FCSTD DOCUMENT  (FreeCAD 0.17R11237 (Git))
Label: Box_Latest
License: All rights reserved
LicenseURL: http://en.wikipedia.org/wiki/All_rights_reserved
objects: Sketcher::SketchObject×1
note: 1 computed .brp shape members not serialized (recipe doc carries the construction recipe); baked Part::Feature solids carry a one-line shape summary decoded from their .brp

FEATURE [Sketcher::SketchObject] Sketch
  sketch-geometry (58):
    g0: LineSegment StartX=-50.2046 StartY=69.3306 StartZ=0 EndX=39.7954 EndY=69.3306 EndZ=0
    g1: LineSegment StartX=39.7954 StartY=69.3306 StartZ=0 EndX=39.7954 EndY=-70.6694 EndZ=0
    g2: LineSegment StartX=39.7954 StartY=-70.6694 StartZ=0 EndX=-50.2046 EndY=-70.6694 EndZ=0
    g3: LineSegment StartX=-50.2046 StartY=-70.6694 StartZ=0 EndX=-50.2046 EndY=69.3306 EndZ=0
    g4: LineSegment StartX=-20 StartY=-57.6694 StartZ=0 EndX=10 EndY=-57.6694 EndZ=0
    g5: LineSegment StartX=10 StartY=-57.6694 StartZ=0 EndX=10 EndY=-53.6694 EndZ=0
    g6: LineSegment StartX=10 StartY=-53.6694 StartZ=0 EndX=-20 EndY=-53.6694 EndZ=0
    g7: LineSegment StartX=-20 StartY=-53.6694 StartZ=0 EndX=-20 EndY=-57.6694 EndZ=0
    g8: LineSegment StartX=-40.7046 StartY=56.7181 StartZ=0 EndX=30.2954 EndY=56.7181 EndZ=0
    g9: LineSegment StartX=30.2954 StartY=56.7181 StartZ=0 EndX=30.2954 EndY=32.7181 EndZ=0
    g10: LineSegment StartX=30.2954 StartY=32.7181 StartZ=0 EndX=-40.7046 EndY=32.7181 EndZ=0
    g11: LineSegment StartX=-40.7046 StartY=32.7181 StartZ=0 EndX=-40.7046 EndY=56.7181 EndZ=0
    g12: LineSegment StartX=49.7553 StartY=63.8027 StartZ=0 EndX=79.7553 EndY=63.8027 EndZ=0
    g13: LineSegment StartX=79.7553 StartY=63.8027 StartZ=0 EndX=79.7553 EndY=-66.1973 EndZ=0
    g14: LineSegment StartX=79.7553 StartY=-66.1973 StartZ=0 EndX=49.7553 EndY=-66.1973 EndZ=0
    g15: LineSegment StartX=49.7553 StartY=-66.1973 StartZ=0 EndX=49.7553 EndY=63.8027 EndZ=0
    g16: LineSegment StartX=-60 StartY=63.8027 StartZ=0 EndX=-90 EndY=63.8027 EndZ=0
    g17: LineSegment StartX=-90 StartY=63.8027 StartZ=0 EndX=-90 EndY=-66.1973 EndZ=0
    g18: LineSegment StartX=-90 StartY=-66.1973 StartZ=0 EndX=-60 EndY=-66.1973 EndZ=0
    g19: LineSegment StartX=-60 StartY=-66.1973 StartZ=0 EndX=-60 EndY=63.8027 EndZ=0
    g20: LineSegment StartX=-50 StartY=80 StartZ=0 EndX=40 EndY=80 EndZ=0
    g21: LineSegment StartX=40 StartY=80 StartZ=0 EndX=40 EndY=110 EndZ=0
    g22: LineSegment StartX=40 StartY=110 StartZ=0 EndX=-50 EndY=110 EndZ=0
    g23: LineSegment StartX=-50 StartY=110 StartZ=0 EndX=-50 EndY=80 EndZ=0
    g24: LineSegment StartX=-50 StartY=-80 StartZ=0 EndX=40 EndY=-80 EndZ=0
    g25: LineSegment StartX=40 StartY=-80 StartZ=0 EndX=40 EndY=-110 EndZ=0
    g26: LineSegment StartX=40 StartY=-110 StartZ=0 EndX=-50 EndY=-110 EndZ=0
    g27: LineSegment StartX=-50 StartY=-110 StartZ=0 EndX=-50 EndY=-80 EndZ=0
    g28: LineSegment StartX=90.013 StartY=70 StartZ=0 EndX=180.013 EndY=70 EndZ=0
    g29: LineSegment StartX=180.013 StartY=70 StartZ=0 EndX=180.013 EndY=-70 EndZ=0
    g30: LineSegment StartX=180.013 StartY=-70 StartZ=0 EndX=90.013 EndY=-70 EndZ=0
    g31: LineSegment StartX=90.013 StartY=-70 StartZ=0 EndX=90.013 EndY=70 EndZ=0
    g32: LineSegment StartX=270.325 StartY=30 StartZ=0 EndX=325.325 EndY=30 EndZ=0
    g33: LineSegment StartX=325.325 StartY=30 StartZ=0 EndX=325.325 EndY=0 EndZ=0
    g34: LineSegment StartX=325.325 StartY=0 StartZ=0 EndX=270.325 EndY=0 EndZ=0
    g35: LineSegment StartX=270.325 StartY=0 StartZ=0 EndX=270.325 EndY=30 EndZ=0
    g36: Circle CenterX=284.825 CenterY=15 CenterZ=0 NormalX=0 NormalY=0 NormalZ=1 Radius=8
    g37: Circle CenterX=310.825 CenterY=15 CenterZ=0 NormalX=0 NormalY=0 NormalZ=1 Radius=8
    g38: LineSegment StartX=254.29 StartY=30 StartZ=0 EndX=229.29 EndY=30 EndZ=0
    g39: LineSegment StartX=229.29 StartY=30 StartZ=0 EndX=229.29 EndY=0 EndZ=0
    g40: LineSegment StartX=229.29 StartY=0 StartZ=0 EndX=254.29 EndY=0 EndZ=0
    g41: LineSegment StartX=254.29 StartY=0 StartZ=0 EndX=254.29 EndY=30 EndZ=0
    g42: LineSegment StartX=338.951 StartY=30 StartZ=0 EndX=363.951 EndY=30 EndZ=0
    g43: LineSegment StartX=363.951 StartY=30 StartZ=0 EndX=363.951 EndY=0 EndZ=0
    g44: LineSegment StartX=363.951 StartY=0 StartZ=0 EndX=338.951 EndY=0 EndZ=0
    g45: LineSegment StartX=338.951 StartY=0 StartZ=0 EndX=338.951 EndY=30 EndZ=0
    g46: LineSegment StartX=269.706 StartY=-19.8559 StartZ=0 EndX=324.706 EndY=-19.8559 EndZ=0
    g47: LineSegment StartX=324.706 StartY=-19.8559 StartZ=0 EndX=324.706 EndY=-44.8559 EndZ=0
    g48: LineSegment StartX=324.706 StartY=-44.8559 StartZ=0 EndX=269.706 EndY=-44.8559 EndZ=0
    g49: LineSegment StartX=269.706 StartY=-44.8559 StartZ=0 EndX=269.706 EndY=-19.8559 EndZ=0
    g50: LineSegment StartX=270.204 StartY=75.1059 StartZ=0 EndX=325.204 EndY=75.1059 EndZ=0
    g51: LineSegment StartX=325.204 StartY=75.1059 StartZ=0 EndX=325.204 EndY=50.1059 EndZ=0
    g52: LineSegment StartX=325.204 StartY=50.1059 StartZ=0 EndX=270.204 EndY=50.1059 EndZ=0
    g53: LineSegment StartX=270.204 StartY=50.1059 StartZ=0 EndX=270.204 EndY=75.1059 EndZ=0
    g54: LineSegment StartX=378.192 StartY=30 StartZ=0 EndX=433.192 EndY=30 EndZ=0
    g55: LineSegment StartX=433.192 StartY=30 StartZ=0 EndX=433.192 EndY=0 EndZ=0
    g56: LineSegment StartX=433.192 StartY=0 StartZ=0 EndX=378.192 EndY=0 EndZ=0
    g57: LineSegment StartX=378.192 StartY=0 StartZ=0 EndX=378.192 EndY=30 EndZ=0
  constraints (176):
    c: Coincident(g0,g1)
    c: Coincident(g1,g2)
    c: Coincident(g2,g3)
    c: Coincident(g3,g0)
    c: Horizontal(g0)
    c: Horizontal(g2)
    c: Vertical(g1)
    c: Vertical(g3)
    c: Coincident(g4,g5)
    c: Coincident(g5,g6)
    c: Coincident(g6,g7)
    c: Coincident(g7,g4)
    c: Horizontal(g4)
    c: Horizontal(g6)
    c: Vertical(g5)
    c: Vertical(g7)
    c: Coincident(g8,g9)
    c: Coincident(g9,g10)
    c: Coincident(g10,g11)
    c: Coincident(g11,g8)
    c: Horizontal(g8)
    c: Horizontal(g10)
    c: Vertical(g9)
    c: Vertical(g11)
    c: Coincident(g12,g13)
    c: Coincident(g13,g14)
    c: Coincident(g14,g15)
    c: Coincident(g15,g12)
    c: Horizontal(g12)
    c: Horizontal(g14)
    c: Vertical(g13)
    c: Vertical(g15)
    c: Coincident(g16,g17)
    c: Coincident(g17,g18)
    c: Coincident(g18,g19)
    c: Coincident(g19,g16)
    c: Horizontal(g16)
    c: Horizontal(g18)
    c: Vertical(g17)
    c: Vertical(g19)
    c: Coincident(g20,g21)
    c: Coincident(g21,g22)
    c: Coincident(g22,g23)
    c: Coincident(g23,g20)
    c: Horizontal(g20)
    c: Horizontal(g22)
    c: Vertical(g21)
    c: Vertical(g23)
    c: Coincident(g24,g25)
    c: Coincident(g25,g26)
    c: Coincident(g26,g27)
    c: Coincident(g27,g24)
    c: Horizontal(g24)
    c: Horizontal(g26)
    c: Vertical(g25)
    c: Vertical(g27)
    c: Horizontal(g12,g16)
    c: Horizontal(g14,g18)
    c: Coincident(g28,g29)
    c: Coincident(g29,g30)
    c: Coincident(g30,g31)
    c: Coincident(g31,g28)
    c: Horizontal(g28)
    c: Horizontal(g30)
    c: Vertical(g31)
    c: DistanceY(g28,g30) = -140
    c: DistanceX(g28,g30) = -90
    c: Coincident(g32,g33)
    c: Coincident(g33,g34)
    c: Coincident(g34,g35)
    c: Coincident(g35,g32)
    c: Horizontal(g32)
    c: Horizontal(g34)
    c: Vertical(g33)
    c: Vertical(g35)
    c: Equal(g15,g19)
    c: Equal(g24,g26)
    c: Equal(g26,g20)
    c: Equal(g20,g22)
    c: Equal(g25,g27)
    c: Equal(g27,g23)
    c: Equal(g23,g21)
    c: Equal(g12,g14)
    c: Equal(g14,g18)
    c: Equal(g18,g16)
    c: Equal(g3,g1)
    c: Equal(g1,g31)
    c: Equal(g31,g29)
    c: Equal(g0,g28)
    c: Equal(g28,g30)
    c: Equal(g30,g2)
    c: Distance(g13) = 130
    c: Equal(g0,g2)
    c: Equal(g2,g24)
    c: Equal(g24,g26)
    c: Equal(g26,g20)
    c: Equal(g20,g22)
    c: Distance(g22) = 90
    c: Equal(g8,g10)
    c: Distance(g8) = 71
    c: Equal(g9,g11)
    c: Distance(g9) = 24
    c: Equal(g25,g14)
    c: Equal(g24,g2)
    c: Distance(g14) = 30
    c: Distance(g32) = 55
    c: Distance(g35) = 30
    c: Equal(g36,g37)
    c: Radius(g37) = 8
    c: Distance(g36,g37) = 26
    c: Distance(g36,g35) = 14.5
    c: Distance(g36,g32) = 15
    c: Horizontal(g36,g37)
    c: Coincident(g38,g39)
    c: Coincident(g39,g40)
    c: Coincident(g40,g41)
    c: Coincident(g41,g38)
    c: Horizontal(g38)
    c: Horizontal(g40)
    c: Vertical(g39)
    c: Vertical(g41)
    c: Coincident(g42,g43)
    c: Coincident(g43,g44)
    c: Coincident(g44,g45)
    c: Coincident(g45,g42)
    c: Horizontal(g42)
    c: Horizontal(g44)
    c: Vertical(g43)
    c: Vertical(g45)
    c: Equal(g45,g43)
    c: Equal(g43,g41)
    c: Equal(g41,g39)
    c: Equal(g39,g33)
    c: Coincident(g46,g47)
    c: Coincident(g47,g48)
    c: Coincident(g48,g49)
    c: Coincident(g49,g46)
    c: Horizontal(g46)
    c: Vertical(g47)
    c: Vertical(g49)
    c: Coincident(g50,g51)
    c: Coincident(g51,g52)
    c: Coincident(g52,g53)
    c: Coincident(g53,g50)
    c: Horizontal(g50)
    c: Horizontal(g52)
    c: Vertical(g51)
    c: Vertical(g53)
    c: Equal(g46,g50)
    c: Equal(g50,g34)
    c: Equal(g53,g47)
    c: Equal(g47,g49)
    c: Equal(g49,g51)
    c: Equal(g51,g44)
    c: Equal(g44,g42)
    c: Equal(g42,g38)
    c: Equal(g38,g40)
    c: Distance(g42) = 25
    c: Coincident(g54,g55)
    c: Coincident(g55,g56)
    c: Coincident(g56,g57)
    c: Coincident(g57,g54)
    c: Horizontal(g54)
    c: Horizontal(g56)
    c: Vertical(g55)
    c: Vertical(g57)
    c: Equal(g57,g55)
    c: Equal(g55,g33)
    c: Equal(g54,g56)
    c: Equal(g56,g34)
    c: Distance(g4) = 30
    c: Distance(g5) = 4
    c: Distance(g4,g2) = 13
    c: Equal(g3,g1)
    c: Equal(g1,g31)
    c: Distance(g8,g3) = 9.5
